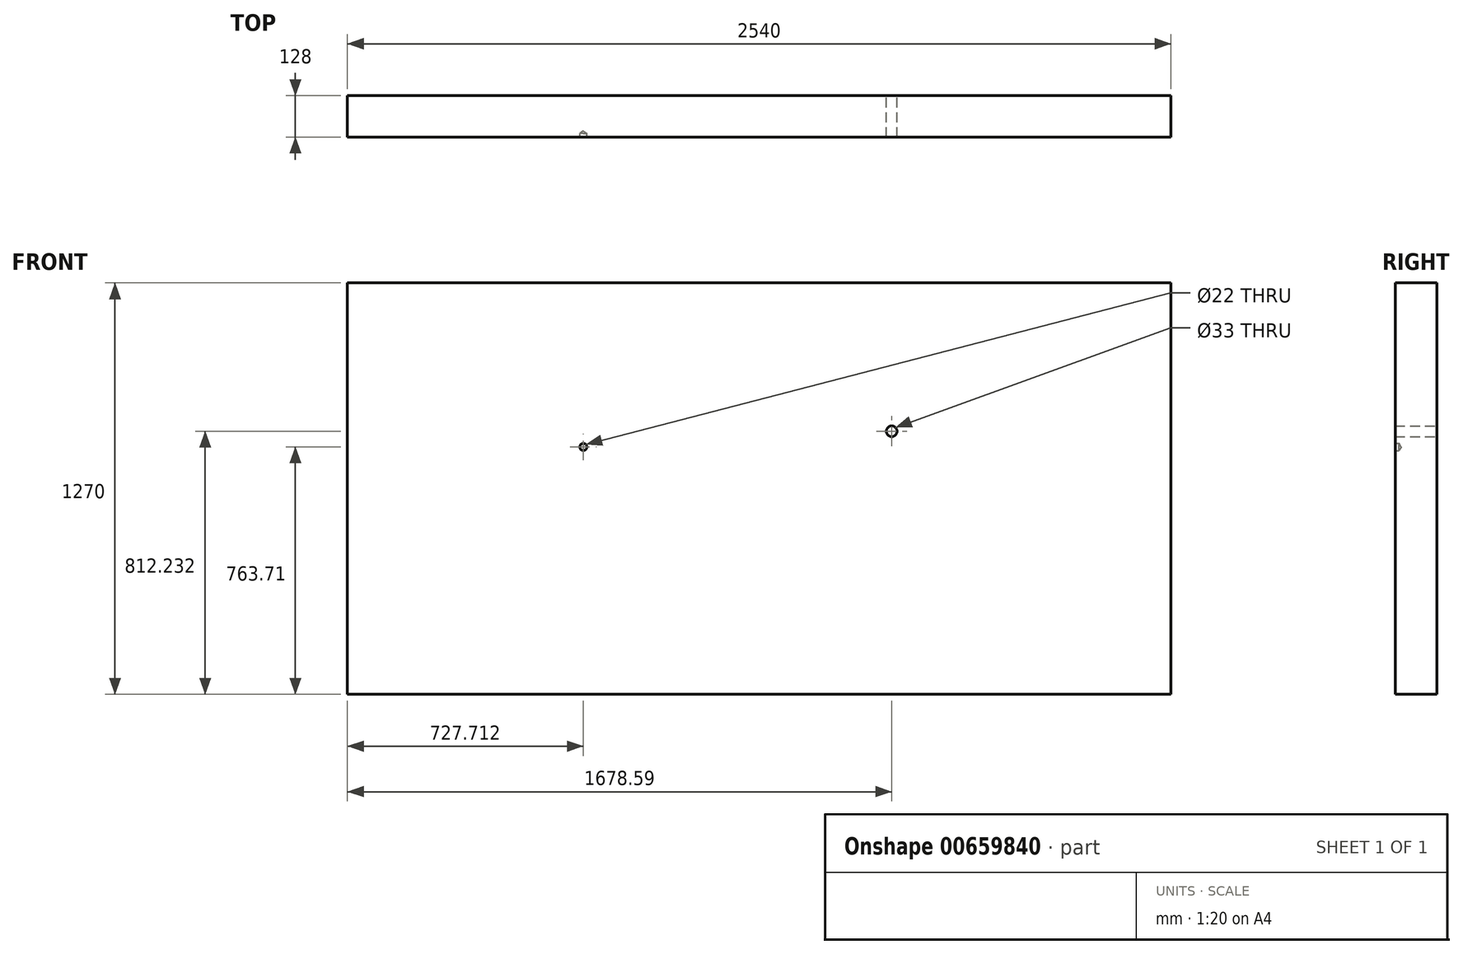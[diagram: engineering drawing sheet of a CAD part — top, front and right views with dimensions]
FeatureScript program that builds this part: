
annotation { "Feature Type Name" : "Feature", "Feature Type Description" : "" }
export const myFeature = defineFeature(function(context is Context, id is Id, definition is map)
    precondition{}
    {
        {
            var Q0;
            Q0=qCreatedBy(makeId("Front.planeOp"),FACE);
            var sketch = newSketch(context, id + "F0", { "sketchPlane" : qUnion([Q0])});
            skLineSegment(sketch, "E0.bottom", {"start": v(-1266.7, -1101.19) * mm, "end": v(1273.3, -1101.19) * mm});
            skLineSegment(sketch, "E0.top", {"start": v(-1266.7, 168.81) * mm, "end": v(1273.3, 168.81) * mm});
            skLineSegment(sketch, "E0.left", {"start": v(-1266.7, -1101.19) * mm, "end": v(-1266.7, 168.81) * mm});
            skLineSegment(sketch, "E0.right", {"start": v(1273.3, -1101.19) * mm, "end": v(1273.3, 168.81) * mm});
            skSolve(sketch);
        }
        {
            var Q0;
            Q0 = qSketchRegion(id + "F0", true);
            extrude(context, id + "F1", {"entities" : qUnion([Q0]), "depth" : 128 * mm, "offsetDistance" : 25.4 * mm});
        }
        {
            var Q0;
            Q0=makeQuery(id+"F1.opExtrude","CAP_FACE",FACE,{"disambiguationData":[OSD([sQuery(id+"F0.wireOp",EDGE,"E0.bottom"),sQuery(id+"F0.wireOp",EDGE,"E0.top"),sQuery(id+"F0.wireOp",EDGE,"E0.left"),sQuery(id+"F0.wireOp",EDGE,"E0.right")])],"isStart":false});
            var sketch = newSketch(context, id + "F2", { "sketchPlane" : qUnion([Q0])});
            skPoint(sketch, "E1", {"position": v(-538.99, -337.48) * mm});
            skPoint(sketch, "E2", {"position": v(389.82, -334.44) * mm});
            skPoint(sketch, "E3", {"position": v(0, 0) * mm});
            skPoint(sketch, "E4", {"position": v(796.63, 0) * mm});
            skPoint(sketch, "E5", {"position": v(-1617.74, -640.15) * mm});
            skSolve(sketch);
        }
        {
            var Q0;
            Q0=sQuery(id+"F2.wireOp",VERTEX,"E1");
            var Q1;
            Q1=makeQuery(id+"F1.opExtrude","SWEPT_BODY",BODY,{"disambiguationData":[OSD([sQuery(id+"F0.wireOp",EDGE,"E0.bottom"),sQuery(id+"F0.wireOp",EDGE,"E0.top"),sQuery(id+"F0.wireOp",EDGE,"E0.left"),sQuery(id+"F0.wireOp",EDGE,"E0.right")])]});
            hole(context, id + "F3", {"style" : HoleStyle.SIMPLE, "endStyle" : HoleEndStyle.BLIND, "standardTappedOrClearance" : lookupTablePath({ "fit" : "Normal", "standard" : "ISO", "size" : "M20", "type" : "Clearance" }), "standardBlindInLast" : lookupTablePath({ "fit" : "Standard", "standard" : "ISO", "size" : "M20", "type" : "Clearance" }), "holeDiameter" : 22 * mm, "majorDiameter" : 5 * mm, "holeDepth" : 12 * mm, "isTappedThrough" : true, "tappedDepth" : 12 * mm, "tapClearance" : 3, "locations" : qUnion([Q0]), "scope" : qUnion([Q1]), "startStyle" : HoleStartStyle.SKETCH});
        }
        {
            var Q0;
            Q0=makeQuery(id+"F1.opExtrude","CAP_FACE",FACE,{"disambiguationData":[OSD([sQuery(id+"F0.wireOp",EDGE,"E0.bottom"),sQuery(id+"F0.wireOp",EDGE,"E0.top"),sQuery(id+"F0.wireOp",EDGE,"E0.left"),sQuery(id+"F0.wireOp",EDGE,"E0.right")])],"isStart":false});
            var sketch = newSketch(context, id + "F4", { "sketchPlane" : qUnion([Q0])});
            skPoint(sketch, "E6", {"position": v(411.89, -288.96) * mm});
            skSolve(sketch);
        }
        {
            var Q0;
            Q0=sQuery(id+"F4.wireOp",VERTEX,"E6");
            var Q1;
            Q1=makeQuery(id+"F1.opExtrude","SWEPT_BODY",BODY,{"disambiguationData":[OSD([sQuery(id+"F0.wireOp",EDGE,"E0.bottom"),sQuery(id+"F0.wireOp",EDGE,"E0.top"),sQuery(id+"F0.wireOp",EDGE,"E0.left"),sQuery(id+"F0.wireOp",EDGE,"E0.right")])]});
            hole(context, id + "F5", {"style" : HoleStyle.SIMPLE, "endStyle" : HoleEndStyle.THROUGH, "standardTappedOrClearance" : lookupTablePath({ "standard" : "ISO", "size" : "33", "type" : "Drilled" }), "standardBlindInLast" : lookupTablePath({ "standard" : "ISO", "size" : "33", "type" : "Drilled" }), "holeDiameter" : 33 * mm, "majorDiameter" : 5 * mm, "isTappedThrough" : true, "tappedDepth" : 12 * mm, "tapClearance" : 3, "locations" : qUnion([Q0]), "scope" : qUnion([Q1]), "startStyle" : HoleStartStyle.PART});
        }
    });
